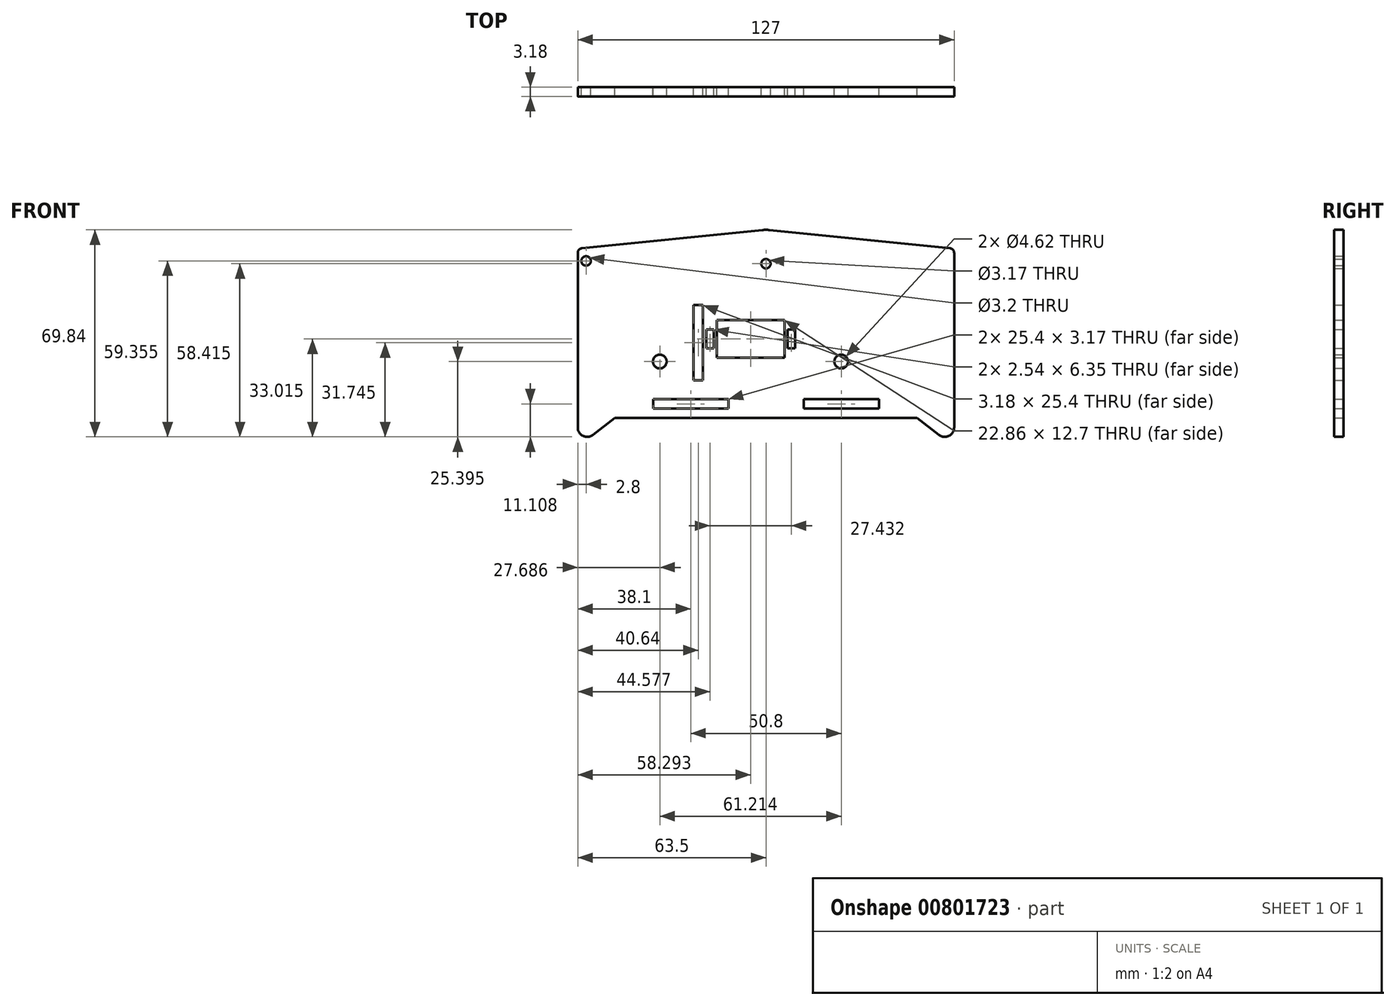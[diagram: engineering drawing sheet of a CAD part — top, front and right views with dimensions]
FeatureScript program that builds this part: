
annotation { "Feature Type Name" : "Feature", "Feature Type Description" : "" }
export const myFeature = defineFeature(function(context is Context, id is Id, definition is map)
    precondition{}
    {
        {
            var Q0;
            Q0=qCreatedBy(makeId("Front.planeOp"),FACE);
            var sketch = newSketch(context, id + "F0", { "sketchPlane" : qUnion([Q0])});
            skLineSegment(sketch, "E0.left", {"start": v(63.5, -31.75) * mm, "end": v(63.5, 27.14) * mm});
            skLineSegment(sketch, "E0.right", {"start": v(-63.5, -28.58) * mm, "end": v(-63.5, 27.14) * mm});
            skPoint(sketch, "E0.middle", {"position": v(0, 0) * mm});
            skCircle(sketch, "E1", {"center": v(0, 23.5) * mm, "radius": 1.59 * mm});
            skPoint(sketch, "E1.centerSnap0", {"position": v(0, 34.93) * mm});
            skArc(sketch, "E2", {"start": v(1.15, 34.86) * mm, "mid": v(0, 34.92) * mm, "end": v(-1.15, 34.86) * mm});
            skPoint(sketch, "E3", {"position": v(-63.5, 28.57) * mm});
            skLineSegment(sketch, "E4", {"start": v(-62.07, 28.72) * mm, "end": v(-1.15, 34.86) * mm});
            skLineSegment(sketch, "E5.MirrorCS", {"start": v(62.07, 28.72) * mm, "end": v(1.15, 34.86) * mm});
            skPoint(sketch, "E6.orphan", {"position": v(-63.5, 34.92) * mm});
            skPoint(sketch, "E7.orphan", {"position": v(63.5, 34.93) * mm});
            skArc(sketch, "E8.filletArc", {"start": v(-62.07, 28.72) * mm, "mid": v(-63.09, 28.2) * mm, "end": v(-63.5, 27.14) * mm});
            skPoint(sketch, "E9.visualSharp", {"position": v(63.5, 28.57) * mm});
            skArc(sketch, "E9.filletArc", {"start": v(63.5, 27.14) * mm, "mid": v(63.09, 28.2) * mm, "end": v(62.07, 28.72) * mm});
            skLineSegment(sketch, "E10.bottom", {"start": v(-38.1, -22.22) * mm, "end": v(-12.7, -22.22) * mm});
            skLineSegment(sketch, "E10.top", {"start": v(-38.1, -25.4) * mm, "end": v(-12.7, -25.4) * mm});
            skLineSegment(sketch, "E10.left", {"start": v(-38.1, -22.22) * mm, "end": v(-38.1, -25.4) * mm});
            skLineSegment(sketch, "E10.right", {"start": v(-12.7, -22.22) * mm, "end": v(-12.7, -25.4) * mm});
            skLineSegment(sketch, "E11.MirrorCS", {"start": v(12.7, -22.23) * mm, "end": v(12.7, -25.4) * mm});
            skLineSegment(sketch, "E12.MirrorCS", {"start": v(38.1, -25.4) * mm, "end": v(12.7, -25.4) * mm});
            skLineSegment(sketch, "E13.MirrorCS", {"start": v(38.1, -22.23) * mm, "end": v(38.1, -25.4) * mm});
            skLineSegment(sketch, "E14.MirrorCS", {"start": v(38.1, -22.23) * mm, "end": v(12.7, -22.23) * mm});
            skLineSegment(sketch, "E15", {"start": v(-50.94, -28.58) * mm, "end": v(50.94, -28.58) * mm});
            skArc(sketch, "E16", {"start": v(-63.5, -31.75) * mm, "mid": v(-61.73, -34.6) * mm, "end": v(-58.4, -34.27) * mm});
            skPoint(sketch, "E16.centerSnap0", {"position": v(-63.5, -31.75) * mm});
            skArc(sketch, "E17.MirrorC", {"start": v(63.5, -31.75) * mm, "mid": v(61.73, -34.6) * mm, "end": v(58.4, -34.27) * mm});
            skLineSegment(sketch, "E18", {"start": v(-58.4, -34.27) * mm, "end": v(-50.94, -28.57) * mm});
            skLineSegment(sketch, "E19.MirrorCS", {"start": v(58.4, -34.27) * mm, "end": v(50.94, -28.57) * mm});
            skPoint(sketch, "E20.orphan", {"position": v(-63.5, -34.93) * mm});
            skPoint(sketch, "E21.orphan", {"position": v(63.5, -34.92) * mm});
            skLineSegment(sketch, "E22", {"start": v(-63.5, -28.58) * mm, "end": v(-63.5, -31.75) * mm});
            skPoint(sketch, "E23.centerSnap0", {"position": v(-25.4, -22.22) * mm});
            skCircle(sketch, "E24", {"center": v(25.4, -9.53) * mm, "radius": 2.31 * mm});
            skPoint(sketch, "E24.centerSnap0", {"position": v(25.4, -22.23) * mm});
            skCircle(sketch, "E25", {"center": v(-60.7, 24.43) * mm, "radius": 1.6 * mm});
            skLineSegment(sketch, "E26.top", {"start": v(5.97, 4.45) * mm, "end": v(-16.38, 4.45) * mm});
            skPoint(sketch, "E26.middle", {"position": v(-5.2, 12.45) * mm});
            skPoint(sketch, "E27.centerSnap0", {"position": v(5.97, 20.07) * mm});
            skLineSegment(sketch, "E28", {"start": v(-16.38, -8.25) * mm, "end": v(5.97, -8.25) * mm});
            skCircle(sketch, "E29.MirrorC", {"center": v(-35.81, -9.53) * mm, "radius": 2.31 * mm});
            skPoint(sketch, "E30.start.orphan", {"position": v(-5.2, -8.25) * mm});
            skLineSegment(sketch, "E31.bottom", {"start": v(9.78, -5.08) * mm, "end": v(7.24, -5.08) * mm});
            skLineSegment(sketch, "E31.top", {"start": v(9.78, 1.27) * mm, "end": v(7.24, 1.27) * mm});
            skLineSegment(sketch, "E31.left", {"start": v(9.78, -5.08) * mm, "end": v(9.78, 1.27) * mm});
            skLineSegment(sketch, "E31.right", {"start": v(7.24, -5.08) * mm, "end": v(7.24, 1.27) * mm});
            skPoint(sketch, "E31.middle", {"position": v(8.5, -1.9) * mm});
            skPoint(sketch, "E31.middle.positionSnap0", {"position": v(8.5, 5.72) * mm});
            skPoint(sketch, "E31.middle.positionSnap1", {"position": v(9.78, -1.9) * mm});
            skPoint(sketch, "E31.centerSnap0", {"position": v(8.5, 5.72) * mm});
            skPoint(sketch, "E31.centerSnap1", {"position": v(9.78, -1.9) * mm});
            skLineSegment(sketch, "E32.MirrorCS", {"start": v(-17.65, -5.08) * mm, "end": v(-17.65, 1.27) * mm});
            skLineSegment(sketch, "E33.MirrorCS", {"start": v(-20.2, -5.08) * mm, "end": v(-17.65, -5.08) * mm});
            skLineSegment(sketch, "E34.MirrorCS", {"start": v(-20.2, -5.08) * mm, "end": v(-20.2, 1.27) * mm});
            skLineSegment(sketch, "E35.MirrorCS", {"start": v(-20.2, 1.27) * mm, "end": v(-17.65, 1.27) * mm});
            skLineSegment(sketch, "E36", {"start": v(-16.38, 4.45) * mm, "end": v(-16.64, 4.45) * mm});
            skLineSegment(sketch, "E37.bottom", {"start": v(-16.64, 4.45) * mm, "end": v(6.22, 4.45) * mm});
            skLineSegment(sketch, "E37.top", {"start": v(-16.64, -8.25) * mm, "end": v(6.22, -8.25) * mm});
            skLineSegment(sketch, "E37.left", {"start": v(-16.64, 4.45) * mm, "end": v(-16.64, -8.25) * mm});
            skLineSegment(sketch, "E37.right", {"start": v(6.22, 4.45) * mm, "end": v(6.22, -8.25) * mm});
            skPoint(sketch, "E38.start.orphan", {"position": v(-5.2, 4.45) * mm});
            skPoint(sketch, "E39", {"position": v(-22.86, -3.17) * mm});
            skLineSegment(sketch, "E40", {"start": v(-22.86, -15.87) * mm, "end": v(-21.27, -15.87) * mm});
            skLineSegment(sketch, "E41", {"start": v(-21.27, -15.87) * mm, "end": v(-21.27, 9.53) * mm});
            skLineSegment(sketch, "E42", {"start": v(-21.27, 9.53) * mm, "end": v(-24.45, 9.53) * mm});
            skLineSegment(sketch, "E43", {"start": v(-24.45, 9.53) * mm, "end": v(-24.45, -15.87) * mm});
            skLineSegment(sketch, "E44", {"start": v(-24.45, -15.87) * mm, "end": v(-22.86, -15.87) * mm});
            skLineSegment(sketch, "E45", {"start": v(-22.86, -3.17) * mm, "end": v(-22.86, -15.87) * mm});
            skSolve(sketch);
        }
        {
            var Q0;
            Q0 = qSketchRegion(id + "F0", true);
            extrude(context, id + "F1", {"entities" : qUnion([Q0]), "depth" : 3.17 * mm, "offsetDistance" : 25.4 * mm});
        }
    });
